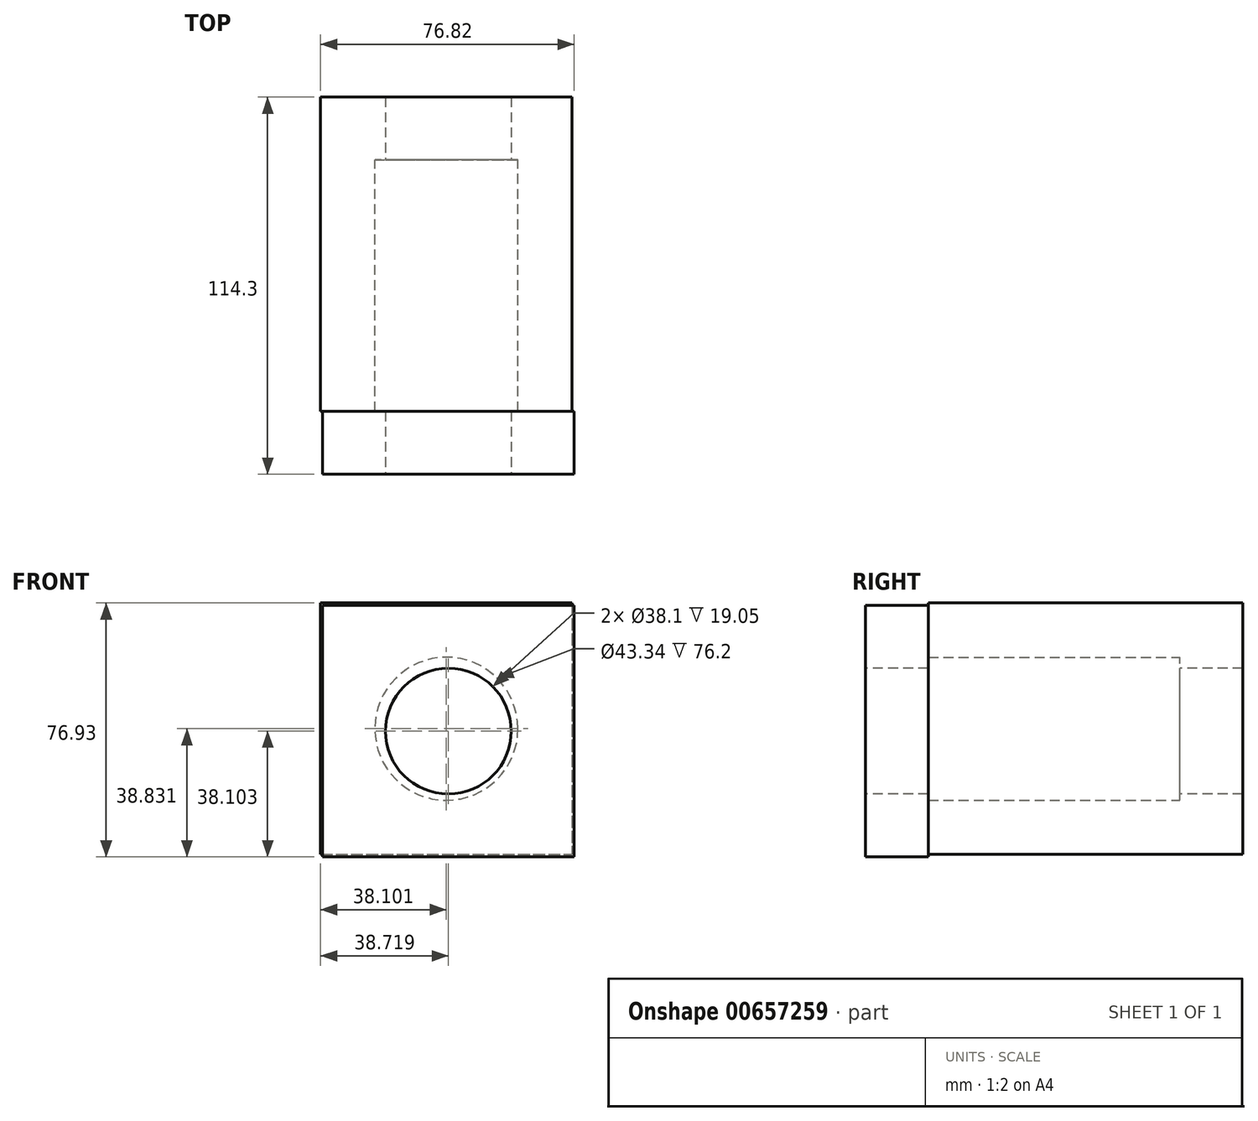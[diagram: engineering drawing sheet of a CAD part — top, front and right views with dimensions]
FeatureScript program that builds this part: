
annotation { "Feature Type Name" : "Feature", "Feature Type Description" : "" }
export const myFeature = defineFeature(function(context is Context, id is Id, definition is map)
    precondition{}
    {
        {
            var Q0;
            Q0=qCreatedBy(makeId("Front.planeOp"),FACE);
            var sketch = newSketch(context, id + "F0", { "sketchPlane" : qUnion([Q0])});
            skLineSegment(sketch, "E0.bottom", {"start": v(-61.36, 39.27) * mm, "end": v(14.84, 39.27) * mm});
            skLineSegment(sketch, "E0.top", {"start": v(-61.36, -36.93) * mm, "end": v(14.84, -36.93) * mm});
            skLineSegment(sketch, "E0.left", {"start": v(-61.36, 39.27) * mm, "end": v(-61.36, -36.93) * mm});
            skLineSegment(sketch, "E0.right", {"start": v(14.84, 39.27) * mm, "end": v(14.84, -36.93) * mm});
            skSolve(sketch);
        }
        {
            var Q0;
            Q0 = qSketchRegion(id + "F0", true);
            extrude(context, id + "F1", {"entities" : qUnion([Q0]), "oppositeDirection" : true, "depth" : 19.05 * mm, "offsetDistance" : 25.4 * mm});
        }
        {
            var Q0;
            Q0=makeQuery(id+"F1.opExtrude","CAP_FACE",FACE,{"disambiguationData":[OSD([sQuery(id+"F0.wireOp",EDGE,"E0.bottom"),sQuery(id+"F0.wireOp",EDGE,"E0.top"),sQuery(id+"F0.wireOp",EDGE,"E0.left"),sQuery(id+"F0.wireOp",EDGE,"E0.right")])],"isStart":true});
            var sketch = newSketch(context, id + "F2", { "sketchPlane" : qUnion([Q0])});
            skLineSegment(sketch, "E1", {"start": v(14.84, -36.93) * mm, "end": v(-61.36, 39.27) * mm});
            skCircle(sketch, "E2", {"center": v(-23.26, 1.17) * mm, "radius": 21.67 * mm});
            skSolve(sketch);
        }
        {
            var Q0;
            {var subQ0=sQuery(id+"F2.wireOp",EDGE,"E2");var subQ1=sQuery(id+"F2.wireOp",EDGE,"E1");var subQ2=makeQuery(id+"F2.imprint","INTERSECT",VERTEX,{"disambiguationData":[OD(0.0)],"derivedFrom":[subQ1,subQ0]});Q0=makeQuery(id+"F2.imprint","IMPRINT",FACE,{"disambiguationData":[TD([[makeQuery(id+"F2.imprint","IMPRINT",EDGE,{"disambiguationData":[TD([[subQ2,-1.0]])],"derivedFrom":subQ1}),-1.0]])]});}
            var Q1;
            {var subQ0=sQuery(id+"F2.wireOp",EDGE,"E2");var subQ1=sQuery(id+"F2.wireOp",EDGE,"E1");var subQ2=makeQuery(id+"F2.imprint","INTERSECT",VERTEX,{"disambiguationData":[OD(0.0)],"derivedFrom":[subQ1,subQ0]});Q1=makeQuery(id+"F2.imprint","IMPRINT",FACE,{"disambiguationData":[TD([[makeQuery(id+"F2.imprint","IMPRINT",EDGE,{"disambiguationData":[TD([[subQ2,-1.0]])],"derivedFrom":subQ1}),1.0]])]});}
            var Q2;
            Q2=sQuery(id+"F2.wireOp",EDGE,"E2");
            extrude(context, id + "F3", {"entities" : qUnion([Q0, Q1]), "operationType" : NewBodyOperationType.ADD, "surfaceEntities" : qUnion([Q2]), "depth" : 76.2 * mm, "offsetDistance" : 25.4 * mm});
        }
        {
            var Q0;
            Q0=makeQuery(id+"F3.opExtrude","CAP_FACE",FACE,{"disambiguationData":[OSD([sQuery(id+"F2.wireOp",EDGE,"E2")])],"isStart":false});
            var sketch = newSketch(context, id + "F4", { "sketchPlane" : qUnion([Q0])});
            skLineSegment(sketch, "E3.bottom", {"start": v(15.46, 38.54) * mm, "end": v(-60.74, 38.54) * mm});
            skLineSegment(sketch, "E3.top", {"start": v(15.46, -37.66) * mm, "end": v(-60.74, -37.66) * mm});
            skLineSegment(sketch, "E3.left", {"start": v(15.46, 38.54) * mm, "end": v(15.46, -37.66) * mm});
            skLineSegment(sketch, "E3.right", {"start": v(-60.74, 38.54) * mm, "end": v(-60.74, -37.66) * mm});
            skSolve(sketch);
        }
        {
            var Q0;
            Q0 = qSketchRegion(id + "F4", true);
            var Q1;
            Q1=makeQuery(id+"F4.imprint","IMPRINT",FACE,{"disambiguationData":[TD([[makeQuery(id+"F4.imprint","IMPRINT",EDGE,{"derivedFrom":makeQuery(id+"F3.opExtrude","CAP_EDGE",EDGE,{"disambiguationData":[OSD([sQuery(id+"F2.wireOp",EDGE,"E2")])],"isStart":false})}),1.0]])]});
            extrude(context, id + "F5", {"entities" : qUnion([Q0, Q1]), "operationType" : NewBodyOperationType.ADD, "depth" : 19.05 * mm, "offsetDistance" : 25.4 * mm});
        }
        {
            var Q0;
            Q0=makeQuery(id+"F5.opExtrude","CAP_FACE",FACE,{"disambiguationData":[OSD([sQuery(id+"F4.wireOp",EDGE,"E3.bottom"),sQuery(id+"F4.wireOp",EDGE,"E3.top"),sQuery(id+"F4.wireOp",EDGE,"E3.left"),sQuery(id+"F4.wireOp",EDGE,"E3.right")])],"isStart":false});
            var sketch = newSketch(context, id + "F6", { "sketchPlane" : qUnion([Q0])});
            skLineSegment(sketch, "E4", {"start": v(15.46, 38.54) * mm, "end": v(-60.74, -37.66) * mm});
            skLineSegment(sketch, "E5", {"start": v(15.46, -33.31) * mm, "end": v(0, -19.53) * mm});
            skLineSegment(sketch, "E6", {"start": v(15.46, -37.66) * mm, "end": v(-60.74, 38.54) * mm});
            skCircle(sketch, "E7", {"center": v(-22.64, 0.44) * mm, "radius": 19.05 * mm});
            skSolve(sketch);
        }
        {
            var Q0;
            Q0 = qSketchRegion(id + "F6", true);
            extrude(context, id + "F7", {"entities" : qUnion([Q0]), "operationType" : NewBodyOperationType.REMOVE, "endBound" : BoundingType.THROUGH_ALL, "oppositeDirection" : true, "depth" : 25.4 * mm, "offsetDistance" : 25.4 * mm});
        }
    });
